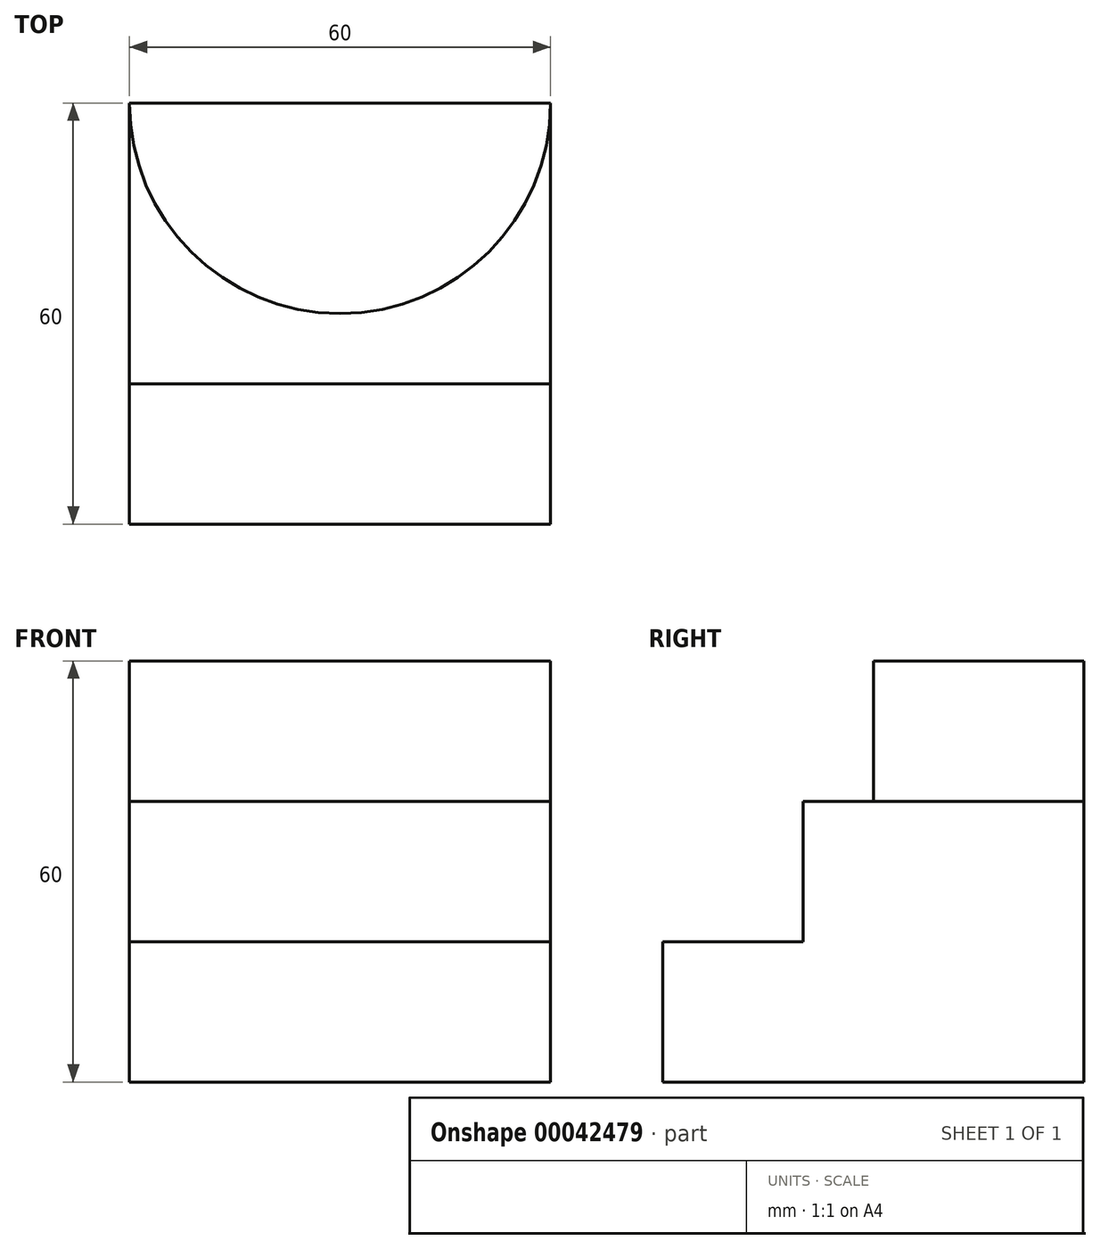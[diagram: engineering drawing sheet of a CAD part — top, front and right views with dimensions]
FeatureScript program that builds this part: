
annotation { "Feature Type Name" : "Feature", "Feature Type Description" : "" }
export const myFeature = defineFeature(function(context is Context, id is Id, definition is map)
    precondition{}
    {
        {
            var Q0;
            Q0=qCreatedBy(makeId("Top.planeOp"),FACE);
            var sketch = newSketch(context, id + "F0", { "sketchPlane" : qUnion([Q0])});
            skLineSegment(sketch, "E0.bottom", {"start": v(0, 0) * mm, "end": v(60, 0) * mm});
            skLineSegment(sketch, "E0.top", {"start": v(0, 60) * mm, "end": v(60, 60) * mm});
            skLineSegment(sketch, "E0.left", {"start": v(0, 0) * mm, "end": v(0, 60) * mm});
            skLineSegment(sketch, "E0.right", {"start": v(60, 0) * mm, "end": v(60, 60) * mm});
            skArc(sketch, "E1", {"start": v(0, 60) * mm, "mid": v(30, 30) * mm, "end": v(60, 60) * mm});
            skLineSegment(sketch, "E2", {"start": v(0, 20) * mm, "end": v(60, 20) * mm});
            skSolve(sketch);
        }
        {
            var Q0;
            Q0=makeQuery(id+"F0.imprint","IMPRINT",FACE,{"disambiguationData":[TD([[makeQuery(id+"F0.imprint","IMPRINT",EDGE,{"derivedFrom":sQuery(id+"F0.wireOp",EDGE,"E0.top")}),-1.0]])]});
            extrude(context, id + "F1", {"entities" : qUnion([Q0]), "depth" : 60 * mm});
        }
        {
            var Q0;
            {var subQ1=sQuery(id+"F0.wireOp",EDGE,"E1");Q0=makeQuery(id+"F0.imprint","IMPRINT",FACE,{"disambiguationData":[TD([[makeQuery(id+"F0.imprint","IMPRINT",EDGE,{"derivedFrom":subQ1}),-1.0]])]});}
            extrude(context, id + "F2", {"entities" : qUnion([Q0]), "operationType" : NewBodyOperationType.ADD, "depth" : 40 * mm});
        }
        {
            var Q0;
            {var subQ2=sQuery(id+"F0.wireOp",EDGE,"E0.bottom");Q0=makeQuery(id+"F0.imprint","IMPRINT",FACE,{"disambiguationData":[TD([[makeQuery(id+"F0.imprint","IMPRINT",EDGE,{"derivedFrom":subQ2}),1.0]])]});}
            extrude(context, id + "F3", {"entities" : qUnion([Q0]), "operationType" : NewBodyOperationType.ADD, "depth" : 20 * mm});
        }
    });
